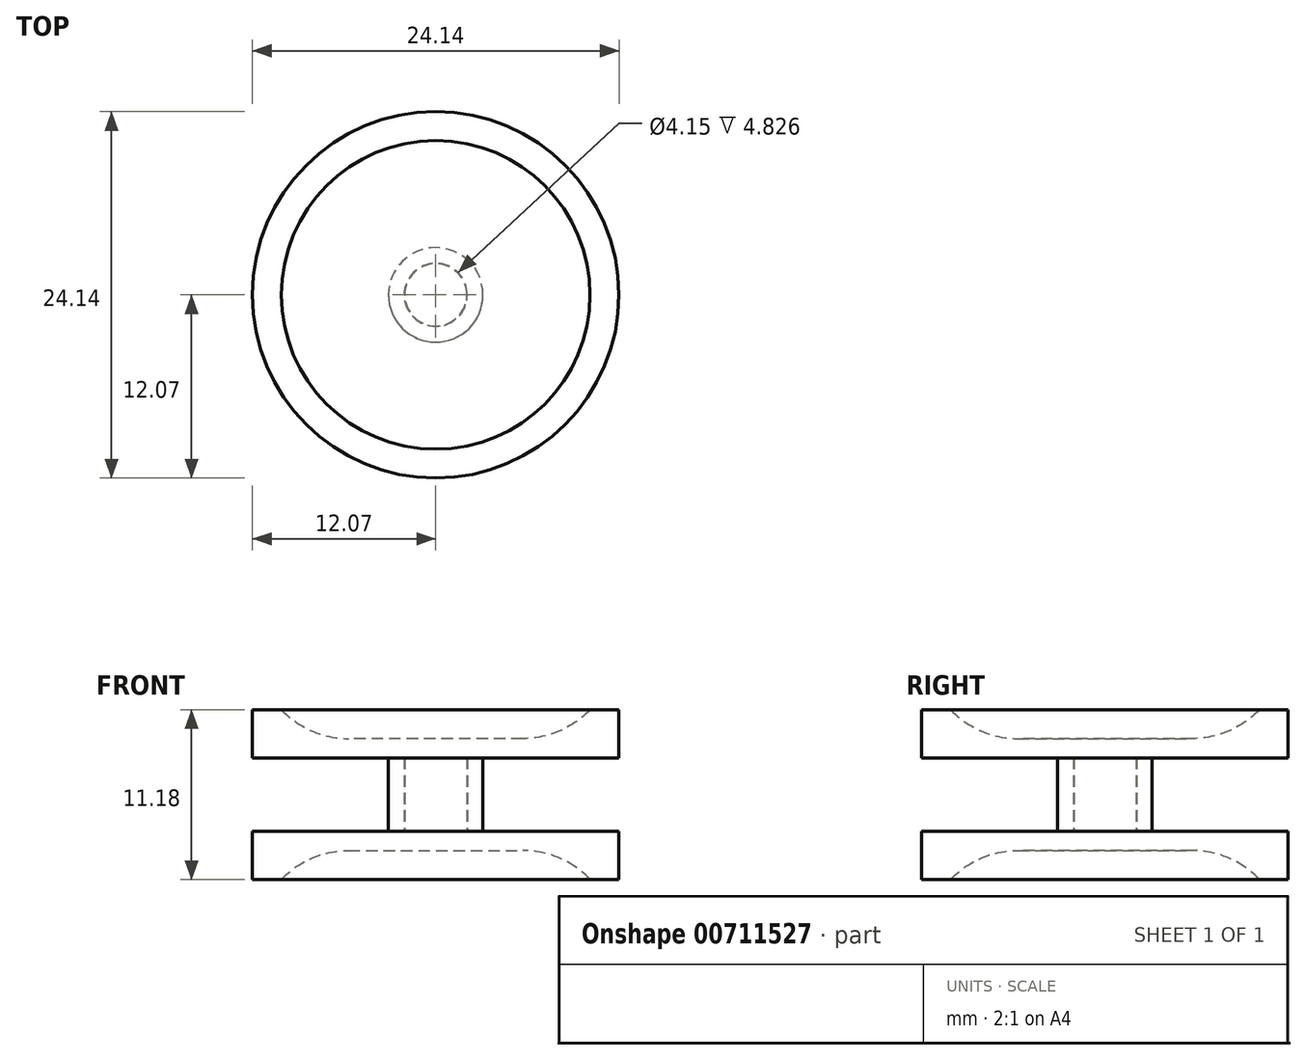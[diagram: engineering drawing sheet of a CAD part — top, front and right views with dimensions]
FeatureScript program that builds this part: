
annotation { "Feature Type Name" : "Feature", "Feature Type Description" : "" }
export const myFeature = defineFeature(function(context is Context, id is Id, definition is map)
    precondition{}
    {
        {
            var Q0;
            Q0=qCreatedBy(makeId("Top.planeOp"),FACE);
            var sketch = newSketch(context, id + "F0", { "sketchPlane" : qUnion([Q0])});
            skCircle(sketch, "E0", {"center": v(0, 0) * mm, "radius": 3.11 * mm});
            skCircle(sketch, "E1", {"center": v(0, 0) * mm, "radius": 2.07 * mm});
            skSolve(sketch);
        }
        {
            var Q0;
            Q0 = qSketchRegion(id + "F0", true);
            extrude(context, id + "F1", {"entities" : qUnion([Q0]), "depth" : 4.83 * mm, "offsetDistance" : 25.4 * mm});
        }
        {
            var Q0;
            Q0=makeQuery(id+"F1.opExtrude","CAP_FACE",FACE,{"disambiguationData":[OSD([sQuery(id+"F0.wireOp",EDGE,"E0"),sQuery(id+"F0.wireOp",EDGE,"E1")])],"isStart":false});
            var sketch = newSketch(context, id + "F2", { "sketchPlane" : qUnion([Q0])});
            skCircle(sketch, "E2", {"center": v(0, 0) * mm, "radius": 12.07 * mm});
            skSolve(sketch);
        }
        {
            var Q0;
            Q0 = qSketchRegion(id + "F2", true);
            extrude(context, id + "F3", {"entities" : qUnion([Q0]), "operationType" : NewBodyOperationType.ADD, "depth" : 3.17 * mm, "offsetDistance" : 25.4 * mm});
        }
        {
            var Q0;
            Q0=makeQuery(id+"F3.opExtrude","CAP_FACE",FACE,{"disambiguationData":[OSD([sQuery(id+"F2.wireOp",EDGE,"E2")])],"isStart":false});
            var sketch = newSketch(context, id + "F4", { "sketchPlane" : qUnion([Q0])});
            skCircle(sketch, "E3", {"center": v(0, 0) * mm, "radius": 10.16 * mm});
            skSolve(sketch);
        }
        {
            var Q0;
            Q0 = qSketchRegion(id + "F4", true);
            extrude(context, id + "F5", {"entities" : qUnion([Q0]), "operationType" : NewBodyOperationType.REMOVE, "oppositeDirection" : true, "depth" : 1.9 * mm, "offsetDistance" : 25.4 * mm});
        }
        {
            var Q0;
            Q0=makeQuery(id+"F1.opExtrude","CAP_FACE",FACE,{"disambiguationData":[OSD([sQuery(id+"F0.wireOp",EDGE,"E0"),sQuery(id+"F0.wireOp",EDGE,"E1")])],"isStart":true});
            var sketch = newSketch(context, id + "F6", { "sketchPlane" : qUnion([Q0])});
            skCircle(sketch, "E4", {"center": v(0, 0) * mm, "radius": 2.05 * mm});
            skSolve(sketch);
        }
        {
            var Q0;
            Q0 = qSketchRegion(id + "F6", true);
            extrude(context, id + "F7", {"entities" : qUnion([Q0]), "oppositeDirection" : true, "depth" : 4.83 * mm, "offsetDistance" : 25.4 * mm});
        }
        {
            var Q0;
            Q0=makeQuery(id+"F7.opExtrude","CAP_FACE",FACE,{"disambiguationData":[OSD([sQuery(id+"F6.wireOp",EDGE,"E4")])],"isStart":true});
            var sketch = newSketch(context, id + "F8", { "sketchPlane" : qUnion([Q0])});
            skCircle(sketch, "E5", {"center": v(0, 0) * mm, "radius": 12.07 * mm});
            skSolve(sketch);
        }
        {
            var Q0;
            Q0 = qSketchRegion(id + "F8", true);
            extrude(context, id + "F9", {"entities" : qUnion([Q0]), "operationType" : NewBodyOperationType.ADD, "depth" : 3.17 * mm, "offsetDistance" : 25.4 * mm});
        }
        {
            var Q0;
            Q0=makeQuery(id+"F9.opExtrude","CAP_FACE",FACE,{"disambiguationData":[OSD([sQuery(id+"F8.wireOp",EDGE,"E5")])],"isStart":false});
            var sketch = newSketch(context, id + "F10", { "sketchPlane" : qUnion([Q0])});
            skCircle(sketch, "E6", {"center": v(0, 0) * mm, "radius": 10.16 * mm});
            skSolve(sketch);
        }
        {
            var Q0;
            Q0 = qSketchRegion(id + "F10", true);
            extrude(context, id + "F11", {"entities" : qUnion([Q0]), "operationType" : NewBodyOperationType.REMOVE, "oppositeDirection" : true, "depth" : 1.9 * mm, "offsetDistance" : 25.4 * mm});
        }
        {
            var Q0;
            Q0=makeQuery(id+"F11.boolean.opBoolean","COPY",EDGE,{"derivedFrom":makeQuery(id+"F11.opExtrude","CAP_EDGE",EDGE,{"disambiguationData":[OSD([sQuery(id+"F10.wireOp",EDGE,"E6")])],"isStart":false})});
            var Q1;
            Q1=makeQuery(id+"F5.boolean.opBoolean","COPY",EDGE,{"derivedFrom":makeQuery(id+"F5.opExtrude","CAP_EDGE",EDGE,{"disambiguationData":[OSD([sQuery(id+"F4.wireOp",EDGE,"E3")])],"isStart":false})});
            fillet(context, id + "F12", {"entities" : qUnion([Q0, Q1]), "radius" : 6.1 * mm, "tangentPropagation" : true, "allowEdgeOverflow" : false});
        }
    });
